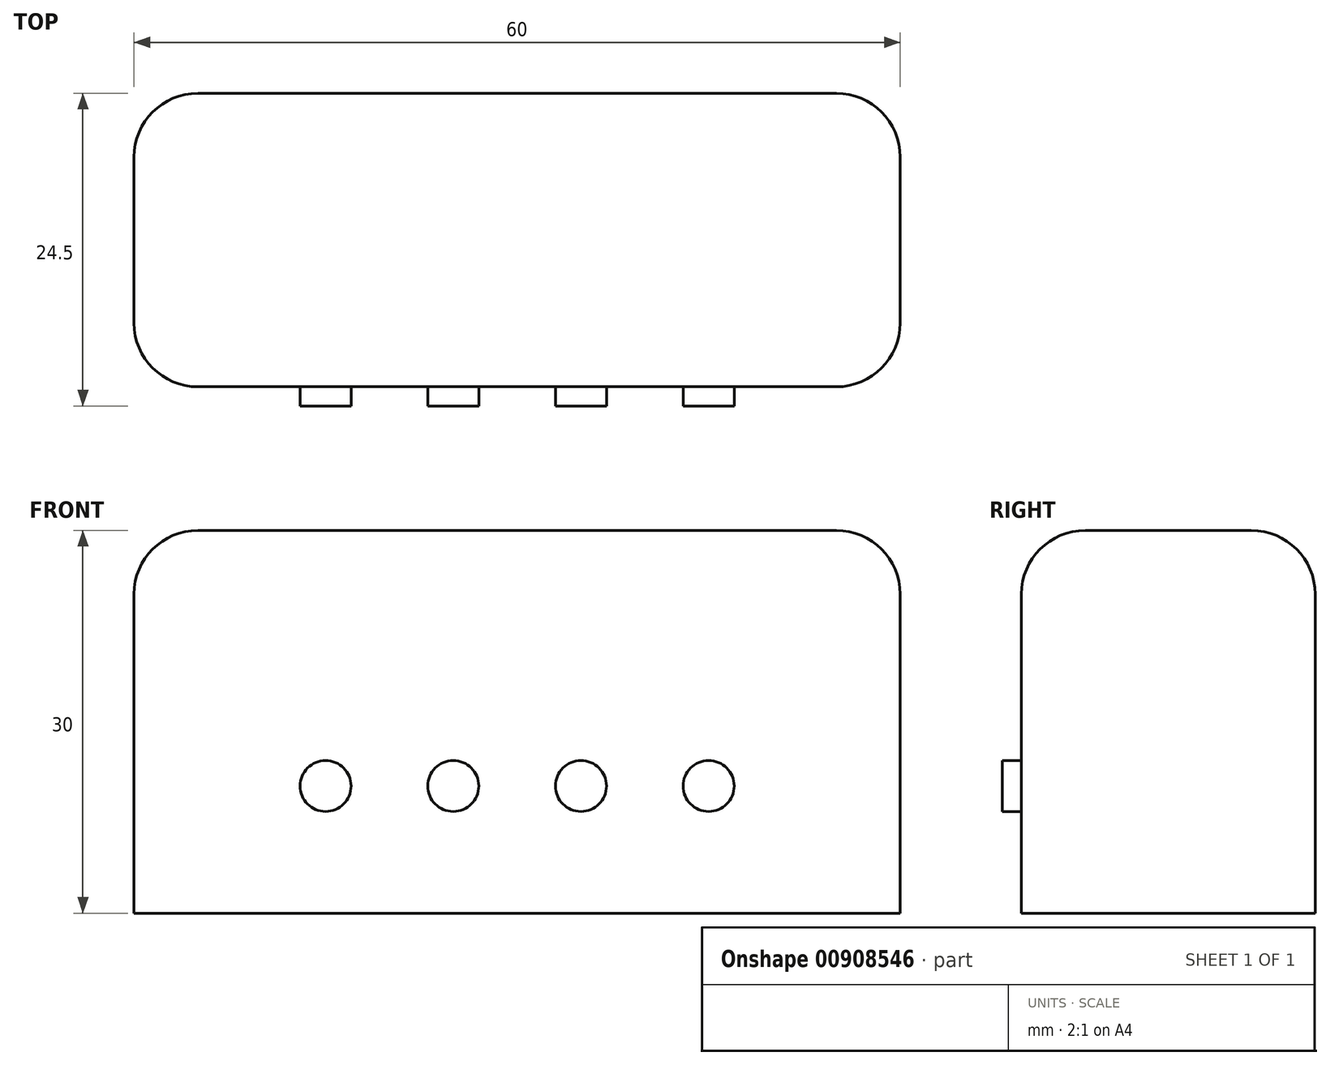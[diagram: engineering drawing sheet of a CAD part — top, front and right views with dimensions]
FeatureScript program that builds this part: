
annotation { "Feature Type Name" : "Feature", "Feature Type Description" : "" }
export const myFeature = defineFeature(function(context is Context, id is Id, definition is map)
    precondition{}
    {
        {
            var Q0;
            Q0=qCreatedBy(makeId("Top.planeOp"),FACE);
            var sketch = newSketch(context, id + "F0", { "sketchPlane" : qUnion([Q0])});
            skLineSegment(sketch, "E0.bottom", {"start": v(-30, 11.5) * mm, "end": v(30, 11.5) * mm});
            skLineSegment(sketch, "E0.top", {"start": v(-30, -11.5) * mm, "end": v(30, -11.5) * mm});
            skLineSegment(sketch, "E0.left", {"start": v(-30, 11.5) * mm, "end": v(-30, -11.5) * mm});
            skLineSegment(sketch, "E0.right", {"start": v(30, 11.5) * mm, "end": v(30, -11.5) * mm});
            skPoint(sketch, "E0.middle", {"position": v(0, 0) * mm});
            skSolve(sketch);
        }
        {
            var Q0;
            Q0=makeQuery(id+"F0.imprint","IMPRINT",FACE,{"disambiguationData":[TD([[makeQuery(id+"F0.imprint","IMPRINT",EDGE,{"derivedFrom":sQuery(id+"F0.wireOp",EDGE,"E0.bottom")}),-1.0]])]});
            extrude(context, id + "F1", {"entities" : qUnion([Q0]), "depth" : 30 * mm, "offsetDistance" : 25 * mm});
        }
        {
            var Q0;
            Q0=makeQuery(id+"F1.opExtrude","SWEPT_EDGE",EDGE,{"disambiguationData":[OSD([sQuery(id+"F0.wireOp",EDGE,"E0.bottom"),sQuery(id+"F0.wireOp",EDGE,"E0.left")])]});
            var Q1;
            Q1=makeQuery(id+"F1.opExtrude","SWEPT_EDGE",EDGE,{"disambiguationData":[OSD([sQuery(id+"F0.wireOp",EDGE,"E0.top"),sQuery(id+"F0.wireOp",EDGE,"E0.left")])]});
            var Q2;
            Q2=makeQuery(id+"F1.opExtrude","SWEPT_EDGE",EDGE,{"disambiguationData":[OSD([sQuery(id+"F0.wireOp",EDGE,"E0.top"),sQuery(id+"F0.wireOp",EDGE,"E0.right")])]});
            var Q3;
            Q3=makeQuery(id+"F1.opExtrude","SWEPT_EDGE",EDGE,{"disambiguationData":[OSD([sQuery(id+"F0.wireOp",EDGE,"E0.bottom"),sQuery(id+"F0.wireOp",EDGE,"E0.right")])]});
            var Q4;
            Q4=makeQuery(id+"F1.opExtrude","CAP_EDGE",EDGE,{"disambiguationData":[OSD([sQuery(id+"F0.wireOp",EDGE,"E0.top")])],"isStart":false});
            var Q5;
            Q5=makeQuery(id+"F1.opExtrude","CAP_EDGE",EDGE,{"disambiguationData":[OSD([sQuery(id+"F0.wireOp",EDGE,"E0.left")])],"isStart":false});
            var Q6;
            Q6=makeQuery(id+"F1.opExtrude","CAP_EDGE",EDGE,{"disambiguationData":[OSD([sQuery(id+"F0.wireOp",EDGE,"E0.bottom")])],"isStart":false});
            var Q7;
            Q7=makeQuery(id+"F1.opExtrude","CAP_EDGE",EDGE,{"disambiguationData":[OSD([sQuery(id+"F0.wireOp",EDGE,"E0.right")])],"isStart":false});
            fillet(context, id + "F2", {"entities" : qUnion([Q0, Q1, Q2, Q3, Q4, Q5, Q6, Q7]), "radius" : 5 * mm, "tangentPropagation" : true, "allowEdgeOverflow" : false});
        }
        {
            var Q0;
            Q0=qCreatedBy(makeId("Front.planeOp"),FACE);
            var sketch = newSketch(context, id + "F3", { "sketchPlane" : qUnion([Q0])});
            skCircle(sketch, "E1", {"center": v(-15, 9.96) * mm, "radius": 2 * mm});
            skLineSegment(sketch, "E2", {"start": v(-15, 9.96) * mm, "end": v(0, 9.96) * mm});
            skLineSegment(sketch, "E3", {"start": v(0, 9.96) * mm, "end": v(15, 9.96) * mm});
            skCircle(sketch, "E4", {"center": v(15, 9.96) * mm, "radius": 2 * mm});
            skCircle(sketch, "E5", {"center": v(-5, 9.96) * mm, "radius": 2 * mm});
            skCircle(sketch, "E6", {"center": v(5, 9.96) * mm, "radius": 2 * mm});
            skSolve(sketch);
        }
        {
            var Q0;
            Q0 = qSketchRegion(id + "F3", true);
            extrude(context, id + "F4", {"entities" : qUnion([Q0]), "operationType" : NewBodyOperationType.ADD, "depth" : 13 * mm, "offsetDistance" : 25 * mm});
        }
    });
